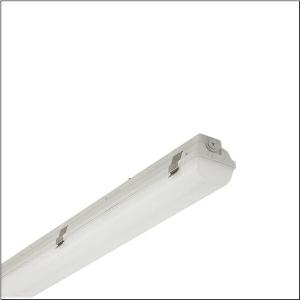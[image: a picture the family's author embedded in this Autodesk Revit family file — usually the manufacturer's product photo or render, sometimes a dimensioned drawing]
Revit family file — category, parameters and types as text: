
# Revit family: monsun_r__21_eco_51fj10dl45a_5ac6
name_source: partatom
category: Lighting Fixtures
units: mm (PartAtom-declared; Revit-internal decimal feet)

## family parameters
Cut with Voids When Loaded = No
Host = Face
Light Source = No
Part Type = Normal
Room Calculation Point = No
Round Connector Dimension = Use Diameter
Shared = No

## types (1)
- Monsun® 21 Eco (1 x LED, 5100 lm, 36 W, 4000K)
    Apparent Load = 36 VA
    CIE Flux Codes = 41 70 89 90 100
    Color Rendering = 80
    Color Temperature = 4000K
    Default Elevation = 1800 mm
    Description = Monsun® 21 Eco, damp-proof luminaire, primary optical cover: diffuser, of PMMA, frosted, light emission: direct distribution, primary light characteristic: symmetric, installation type: suspended mounting, surface-mounted, LED, rated luminous flux: 5.100lm, luminous efficacy: 142lm/W, light colour: 840, colour temperature: 4000K, control gear: ECG DALI, with terminal, 5-pole, max. 2.5mm², mains connection: 220..240V, AC, 50/60Hz, rated input power: 36W, housing, of glass-fibre reinforced polyester, light grey (RAL 7035), length: 1.277mm, width: 90mm, height: 95mm, clip for enclosure, of spring steel V2A, protection rating (complete): IP66, insulation class (complete): insulation class I (protective earthing), certification: CE, UKCA, protection symbol: D, impact resistance: IK02, permissible operating ambient temperature: -20..+35°C, corresponds to IFS (International Featured Standards) requirements for safety and quality in the food industry, contact your sales advisor before using the luminaires in applications with unclear chemical exposure, large temperature fluctuations or condensation-forming humidity, packaging unit: 1 piece
    Height = 103 mm
    Lamp = 1 x LED
    Lamp Light Flux = 5100 lm
    Lamp Power = 36 W
    Lamp count = 1
    Length = 1277 mm
    Luminous efficacy = 142 lm/W
    Manufacturer = Siteco
    ModVariant = No
    Model = 51FJ10DL45A
    Mounting Place = Ceiling
    Mounting Type = Surface mounted
    Number of Poles = 1
    OnlyDefault = Yes
    Power Factor = 1
    Product Name = Monsun® 21 Eco
    Product group = damp-proof luminaire
    ProductGroupID = 301
    Protection Class = Protection class I
    Protection Degree = IP 66
    RLX_Detail_Level = 1
    RLX_Emergency_Light_Flux = 0 lm
    RLX_Emergency_Type = 0
    RLX_Emergency_Type_DB = No
    RlxData = <blob elided: 33413 chars, md5=a8b9c03e>
    Socket = socket
    Standby Power = 0 W
    System Light Flux = 5100 lm
    System Power = 36 W
    Type Comments = Product without accessories
    Type Image = l_1007218.jpg
    URL = http://relux.com
    VarID = ---
    Voltage = 0 V
    Weight = 0.00 kg
    Width = 90 mm

## geometry (parser evidence)
native form markers: Blend x4, Sweep x13
no freeform markers — native parametric forms only
